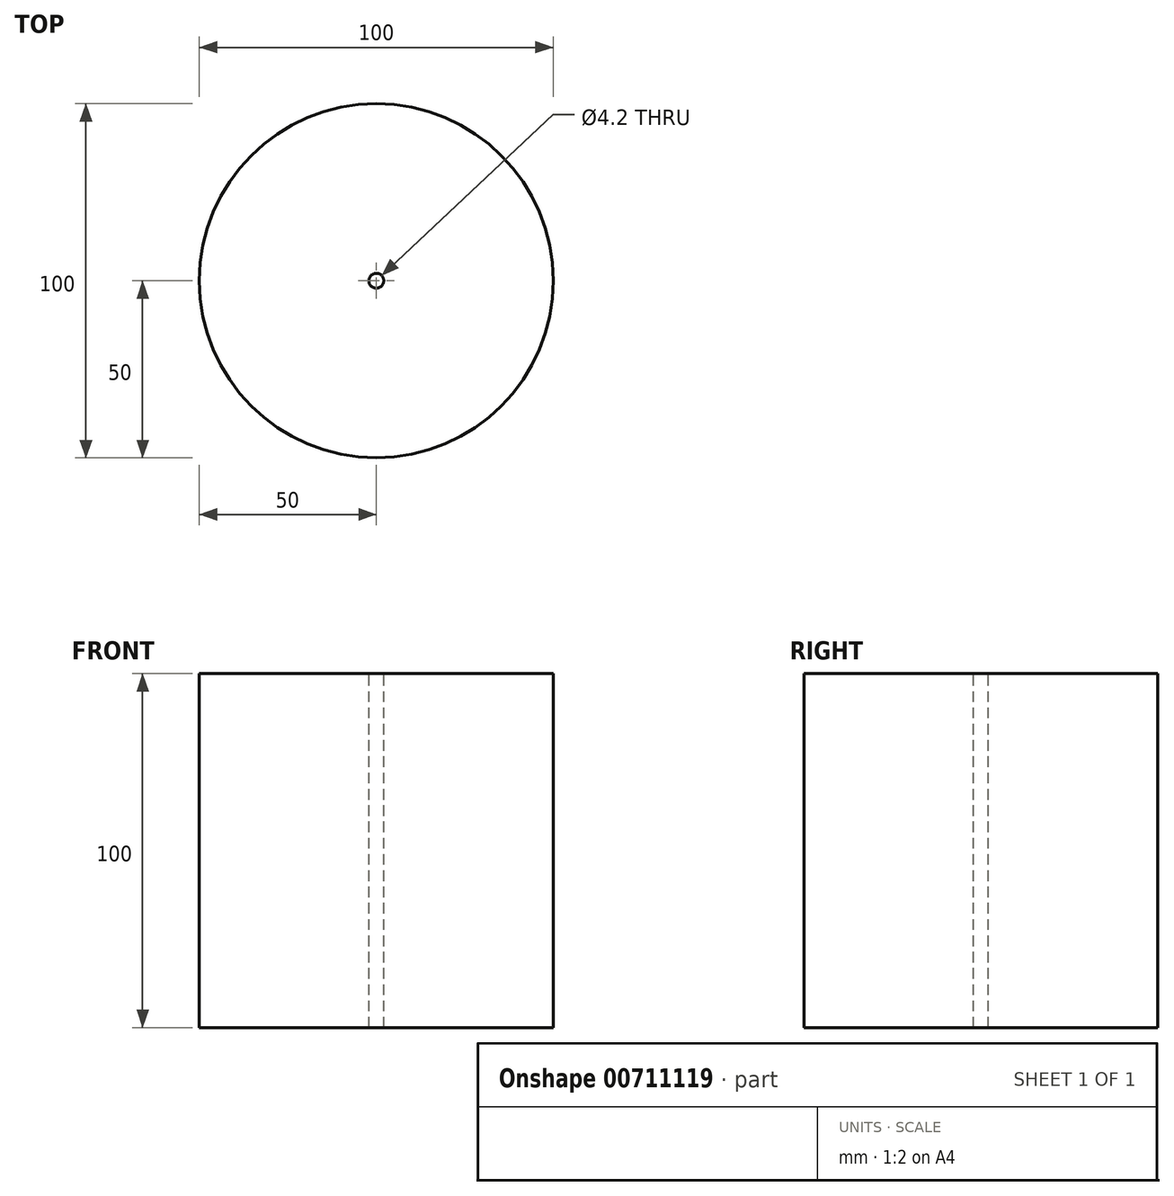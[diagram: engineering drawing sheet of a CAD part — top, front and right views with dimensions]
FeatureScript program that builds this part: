
annotation { "Feature Type Name" : "Feature", "Feature Type Description" : "" }
export const myFeature = defineFeature(function(context is Context, id is Id, definition is map)
    precondition{}
    {
        {
            var Q0;
            Q0=qCreatedBy(makeId("Top.planeOp"),FACE);
            var sketch = newSketch(context, id + "F0", { "sketchPlane" : qUnion([Q0])});
            skCircle(sketch, "E0", {"center": v(0, 0) * mm, "radius": 50 * mm});
            skSolve(sketch);
        }
        {
            var Q0;
            Q0 = qSketchRegion(id + "F0", true);
            extrude(context, id + "F1", {"entities" : qUnion([Q0]), "endBound" : BoundingType.SYMMETRIC, "depth" : 100 * mm, "offsetDistance" : 25 * mm});
        }
        {
            var Q0;
            Q0=makeQuery(id+"F1.opExtrude","CAP_FACE",FACE,{"disambiguationData":[OSD([sQuery(id+"F0.wireOp",EDGE,"E0")])],"isStart":false});
            var sketch = newSketch(context, id + "F2", { "sketchPlane" : qUnion([Q0])});
            skPoint(sketch, "E1", {"position": v(0, 0) * mm});
            skSolve(sketch);
        }
        {
            var Q0;
            Q0=sQuery(id+"F2.wireOp",VERTEX,"E1");
            var Q1;
            Q1=makeQuery(id+"F1.opExtrude","SWEPT_BODY",BODY,{"disambiguationData":[OSD([sQuery(id+"F0.wireOp",EDGE,"E0")])]});
            hole(context, id + "F3", {"style" : HoleStyle.SIMPLE, "endStyle" : HoleEndStyle.THROUGH, "standardTappedOrClearance" : lookupTablePath({ "standard" : "ISO", "engagement" : "75%", "pitch" : "0.8 mm", "size" : "M5", "type" : "Tapped" }), "standardBlindInLast" : lookupTablePath({ "standard" : "ISO", "engagement" : "75%", "pitch" : "0.8 mm", "size" : "M5", "type" : "Tapped" }), "holeDiameter" : 4.2 * mm, "majorDiameter" : 5 * mm, "showTappedDepth" : true, "isTappedThrough" : true, "tappedDepth" : 12 * mm, "tapClearance" : 3, "locations" : qUnion([Q0]), "scope" : qUnion([Q1])});
        }
    });
